# Revit family: IS_iLifeA_T4679_BIM_NL
name_source: partatom
category: Plumbing Fixtures
units: mm (PartAtom-declared; Revit-internal decimal feet)

## family parameters
Always vertical = No
Cut with Voids When Loaded = No
OmniClass Number = 23.45.05.21.11.11
OmniClass Title = Water Operated Water Closets
Part Type = Normal
Room Calculation Point = No
Round Connector Dimension = Use Diameter
Shared = No
Work Plane-Based = No

## types (1)
- T467901 - I.life A sandwich seat for single bowl - White
    Accesoires = https://www.idealstandard.nl
    Accessories = https://www.idealstandard.nl
    Afmetingen = 447 x 35 x 366mm
    AfstandsEenheid = millimeter
    Afwerking = Weiß
    AreaMeasurement = internal
    AreaUnits = Millimeter
    Artikelnummer = T467901
    Artikelomschrijving = I.life A Sandwichsitz für Einzelschüssel - Weiß
    Artikelreferentie = I.life Ein Sandwichsitz für Einzelschüssel
    Auteur = Ideal Standard
    BIMObjectName = IS_IdealStandard_WCseatsandcovers__I.life__T4679
    BIMobject category = Basins
    BIMobject category code = sanitary-basins
    BIMobject main category = Sanitary
    BIMobject main category code = sanitary
    BarCode = 8014140486121
    Barcode = 8014140486121
    Beschrijvinggarantie = Herstellergarantie
    BimObjectNaam = IS_IdealStandard_WCseatsandcovers__I.life__T4679
    Brand = Ideal Standard
    Brand url = http://https:
    Breedte = 0
    BrutoGewicht = 0
    Color = Weiß
    ConnectionType = Plumbing
    Cost = 0 $
    CurrencyUnit = €
    CurrentRevision = 1
    Date of publishing = 28/06/2021
    Description = I.life A Sandwichsitz für Einzelschüssel - Weiß
    Diepte = 0 mm  [stored 0 ft]
    DrainSize = 0 mm  [stored 0 ft]
    DurationUnit = Years
    DuurEenheid = Jaar
    Edition number = 1
    Eigenschappen = Sandwichsitz für Einzelschüssel
    Features = sandwich seat for Single bowl
    Finish = Weiß
    GTIN code = https://8014140486121
    Garantieonderdelen = 5
    Garantieunits = Jaar
    GemaaktOp = 40722
    GrootteAfvoergat = 0
    Help = https://www.idealstandard.nl
    Hoogte = 34.9978319243977
    Hulp = https://www.idealstandard.nl
    IFC Classification = Sanitary Terminal
    IfcExportAs = IfcSanitaryTerminalType
    IfcExportType = WCSEAT
    Installatieinstructies = https://www.idealstandard.nl
    Installation instructions = https://www.idealstandard.nl
    InstallationInstructions = https://www.idealstandard.nl
    Kleur = Weiß
    Kleurwc = Weiß
    Lengte = 447 mm
    LinearUnits = millimeter
    MainColor = White
    MaintenanceInformation = https://www.idealstandard.nl
    Manufacturer = Ideal Standard
    Manufacturer name = Ideal Standard
    ManufacturerURL = https://www.idealstandard.nl
    Masterformat 2014 Code = 33 47 26.16
    Masterformat 2014 Description = Retention Basins
    Materiaal = urea
    MateriaalWC = urea
    Material = urea
    Material main = urea
    Merk = Ideal Standard
    Model = T467901
    ModelNumber = T467901
    ModelReference = I.life A sandwich seat for single bowl
    Montageinstuctie = https://www.idealstandard.nl
    NBS Reference Code = 45-35-70/391
    NBS Reference Description = WC seats and covers
    Name = WCseatsandcovers__I.life__T4679_IdealStandard
    NettWeight = 1.89
    Nettogewicht = 1.89
    NominalDepth = 447 mm
    NominalHeight = 35 mm
    NominalWidth = 366 mm
    Normen = WCseatsandcovers__I.life__T4679_IdealStandard
    OmniClass Code = 23-39 29 13 21 19
    OmniClass Description = Surface Water Retention Basins
    OppervlakteEenheid = Millimeter
    Overloop = 0 mm  [stored 0 ft]
    PanColor = White
    PanMaterial = urea
    Product Guid = 574e3e94-81b0-4fcb-b775-cee2797b3cbd
    Product SKU = T4679
    Product certification = https://www.idealstandard.nl
    Product data url = https://bimobject.com
    Product family = I.life
    Product group = Basin
    Product name = I.life A sandwich seat for single bowl
    Product url = https://www.idealstandard.nl
    ProductInformation = https://www.idealstandard.nl
    ProductSoort = WC-Sitze
    Productinformatie = https://www.idealstandard.nl
    QR code = http://bimobject.com
    Referentie = I.life Ein Sandwichsitz für Einzelschüssel
    Revisie = 1
    Shape = sculpture
    Size = 447 x 35 x 366mm
    Space = Internal
    SpareParts = https://www.idealstandard.nl
    Technical description = https://www.idealstandard.nl
    Telefoonnummer = 077 355 08 08
    ToiletPanType = wallhung bowl
    ToiletType = wallhung bowl
    TypeWC = wallhung bowl
    Typeconnectie = Installation
    TypespoelingWC = abwaschen spülen
    URL = https://https:
    Uniclass 1.4 Code = L7212
    Uniclass 1.4 Description = Washbasins
    Uniclass 2.0 Code = PR-35-79-94
    Uniclass 2.0 Description = Wall-Hung Wash Basins
    Uniclass 2015 Code = Pr_40_20_96_96
    Uniclass 2015 Name = Wall-hung wash basins
    Uniclass2015Beschrijving = WC seats and covers
    Uniclass2015Code = Pr_40_20_93_95
    Uniclass2015Referentie = Pr_40_20_93_95
    Uniclass2015Title = WC seats and covers
    Uniclass2015Version = v1.20
    Urlproducent = https://https:
    ValutaEenheid = €
    Versie = 1
    Version = 1
    Vervangingskosten = 0
    VolumeUnits = Liter
    Volumeunits = Liter
    Vorm = beeldhouwwerk
    WRASURL = https://www.wrasapprovals.co.uk
    WarrantyDescription = manufacturer warranty
    WarrantyDurationParts = 99
    WarrantyDurationUnit = years
    Wisselstukken = https://www.idealstandard.nl
    Youtube clip = https://www.youtube.com

note: [stored X ft] marks values corroborated as IEEE doubles in the binary element streams (Revit-internal decimal feet)

## geometry (parser evidence)
native form markers: Sweep x3
no freeform markers — native parametric forms only
